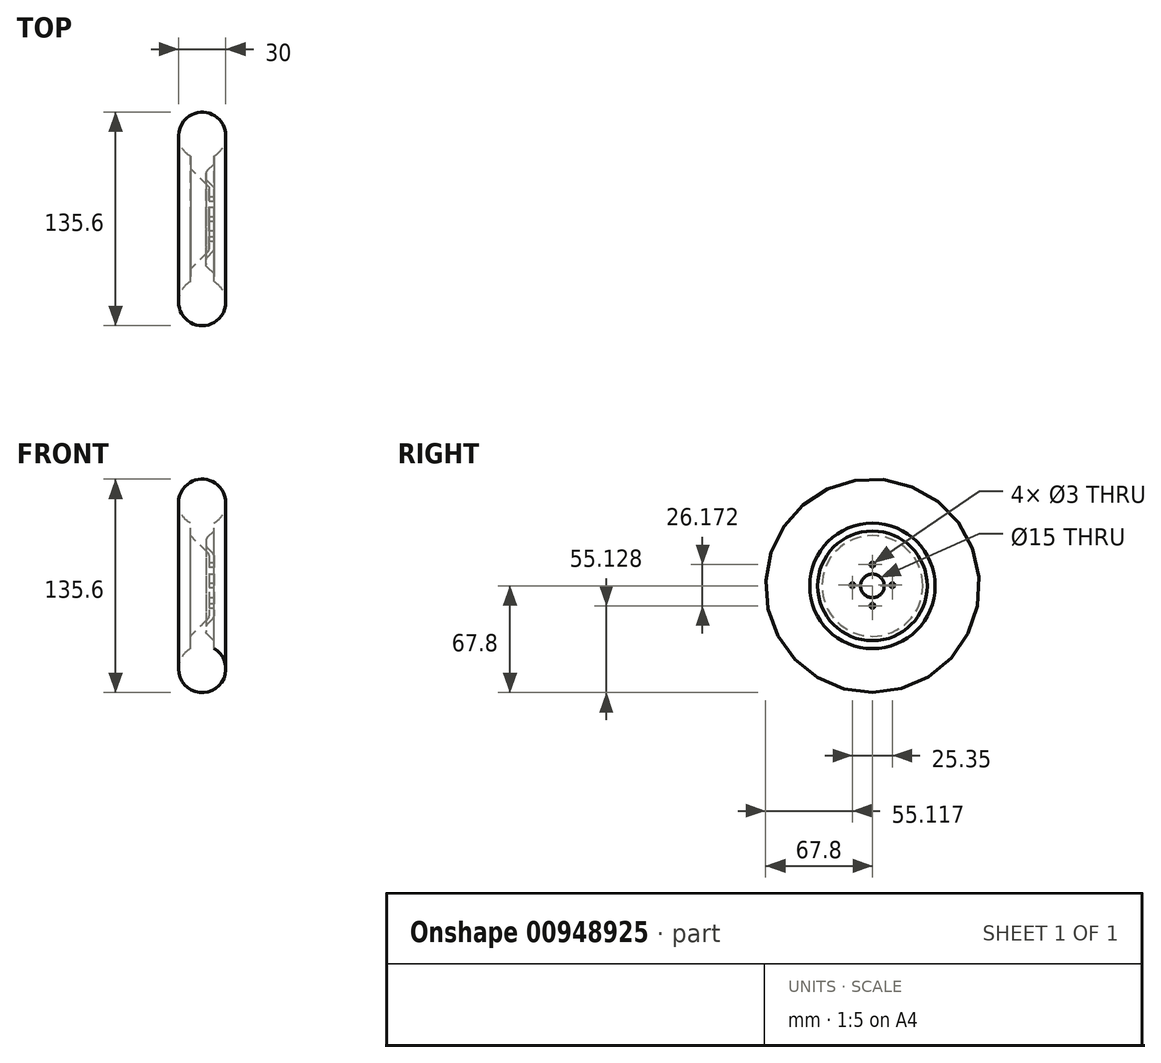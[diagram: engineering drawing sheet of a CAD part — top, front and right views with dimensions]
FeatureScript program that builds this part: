
annotation { "Feature Type Name" : "Feature", "Feature Type Description" : "" }
export const myFeature = defineFeature(function(context is Context, id is Id, definition is map)
    precondition{}
    {
        {
            var Q0;
            Q0=qCreatedBy(makeId("Front.planeOp"),FACE);
            var sketch = newSketch(context, id + "F0", { "sketchPlane" : qUnion([Q0])});
            skArc(sketch, "E0", {"start": v(-28.41, 19.81) * mm, "mid": v(-35.91, 47.8) * mm, "end": v(-43.41, 19.81) * mm});
            skLineSegment(sketch, "E1", {"start": v(-28.41, 19.81) * mm, "end": v(-28.41, 14.81) * mm});
            skLineSegment(sketch, "E2", {"start": v(-33.41, 10) * mm, "end": v(-28.41, 14.81) * mm});
            skLineSegment(sketch, "E3", {"start": v(-33.41, 10) * mm, "end": v(-33.41, 5) * mm});
            skPoint(sketch, "E4.end.orphan", {"position": v(-26.27, 0) * mm});
            skLineSegment(sketch, "E5", {"start": v(-33.41, 5) * mm, "end": v(-28.41, 0) * mm});
            skPoint(sketch, "E6.orphan", {"position": v(-26.27, -38.05) * mm});
            skPoint(sketch, "E7.end.orphan", {"position": v(-37, -38.05) * mm});
            skLineSegment(sketch, "E8", {"start": v(-28.41, 0) * mm, "end": v(-28.41, -20) * mm});
            skLineSegment(sketch, "E9", {"start": v(-61.22, -38.05) * mm, "end": v(-62.94, -38.85) * mm});
            skLineSegment(sketch, "E10", {"start": v(-66.63, -25.87) * mm, "end": v(-67.05, -27.37) * mm});
            skPoint(sketch, "E11.start.orphan", {"position": v(-66.63, -34.7) * mm});
            skPoint(sketch, "E12.end.orphan", {"position": v(-61.22, -34.7) * mm});
            skPoint(sketch, "E13.start.orphan", {"position": v(-37, -25.87) * mm});
            skPoint(sketch, "E14.start.orphan", {"position": v(-47.29, -25.87) * mm});
            skLineSegment(sketch, "E15", {"start": v(-31.41, 0) * mm, "end": v(-31.41, -1.87) * mm});
            skLineSegment(sketch, "E16", {"start": v(-31.41, 0) * mm, "end": v(-43.41, 12) * mm});
            skPoint(sketch, "E17.end.orphan", {"position": v(-52.58, -10.52) * mm});
            skPoint(sketch, "E18.start.orphan", {"position": v(-52.58, -29.68) * mm});
            skLineSegment(sketch, "E19", {"start": v(-28.41, -20) * mm, "end": v(-31.41, -20) * mm});
            skLineSegment(sketch, "E20", {"start": v(-31.41, -20) * mm, "end": v(-31.41, -1.87) * mm});
            skPoint(sketch, "E21.end.orphan", {"position": v(-53, -1.87) * mm});
            skPoint(sketch, "E22.start.orphan", {"position": v(-43.41, 14.81) * mm});
            skLineSegment(sketch, "E23", {"start": v(-43.41, 19.81) * mm, "end": v(-43.41, 12) * mm});
            skPoint(sketch, "E24.start.orphan", {"position": v(-28.41, 32.8) * mm});
            skSolve(sketch);
        }
        {
            var Q0;
            Q0=makeQuery(id+"F0.imprint","IMPRINT",FACE,{"disambiguationData":[TD([[makeQuery(id+"F0.imprint","IMPRINT",EDGE,{"derivedFrom":sQuery(id+"F0.wireOp",EDGE,"ig5zt77j-EQ4V-wuMH-9RIN-2pZxivVrfX0F")}),-1.0]])]});
            var Q1;
            Q1=makeQuery(id+"F0.imprint","IMPRINT",FACE,{"disambiguationData":[TD([[makeQuery(id+"F0.imprint","IMPRINT",EDGE,{"derivedFrom":sQuery(id+"F0.wireOp",EDGE,"ig5zt77j-EQ4V-wuMH-9RIN-2pZxivVrfX0F")}),1.0]])]});
            var Q2;
            Q2=makeQuery(id+"F0.imprint","IMPRINT",FACE,{"disambiguationData":[TD([[makeQuery(id+"F0.imprint","IMPRINT",EDGE,{"derivedFrom":sQuery(id+"F0.wireOp",EDGE,"P19UumjC-ikMn-kLLg-niX1-3UejyW5Ps7u9")}),1.0]])]});
            var Q3;
            Q3=makeQuery(id+"F0.imprint","IMPRINT",FACE,{"disambiguationData":[TD([[makeQuery(id+"F0.imprint","IMPRINT",EDGE,{"derivedFrom":sQuery(id+"F0.wireOp",EDGE,"E8")}),-1.0]])]});
            var Q4;
            Q4=sQuery(id+"F0.wireOp",EDGE,"E19");
            revolve(context, id + "F1", {"surfaceOperationType" : NewSurfaceOperationType.NEW, "entities" : qUnion([Q0, Q1, Q2, Q3]), "axis" : qUnion([Q4]), "revolveType" : RevolveType.FULL});
        }
        {
            var Q0;
            Q0=makeQuery(id+"F1.opRevolve","SWEPT_EDGE",EDGE,{"disambiguationData":[OSD([sQuery(id+"F0.wireOp",EDGE,"E2"),sQuery(id+"F0.wireOp",EDGE,"E3")])]});
            var Q1;
            Q1=makeQuery(id+"F1.opRevolve","SWEPT_EDGE",EDGE,{"disambiguationData":[OSD([sQuery(id+"F0.wireOp",EDGE,"E5"),sQuery(id+"F0.wireOp",EDGE,"E8")])]});
            fillet(context, id + "F2", {"entities" : qUnion([Q0, Q1]), "radius" : 2 * mm, "tangentPropagation" : true, "allowEdgeOverflow" : false});
        }
        {
            var Q0;
            Q0=makeQuery(id+"F1.opRevolve","SWEPT_FACE",FACE,{"disambiguationData":[OSD([sQuery(id+"F0.wireOp",EDGE,"E8")])]});
            var sketch = newSketch(context, id + "F3", { "sketchPlane" : qUnion([Q0])});
            skLineSegment(sketch, "E25", {"start": v(0, 0) * mm, "end": v(0, -20) * mm});
            skCircle(sketch, "E26", {"center": v(0, -20) * mm, "radius": 7.5 * mm});
            skSolve(sketch);
        }
        {
            var Q0;
            Q0=makeQuery(id+"F1.opRevolve","SWEPT_EDGE",EDGE,{"disambiguationData":[OSD([sQuery(id+"F0.wireOp",EDGE,"E3"),sQuery(id+"F0.wireOp",EDGE,"E5")])]});
            fillet(context, id + "F4", {"entities" : qUnion([Q0]), "radius" : 1.9 * mm, "tangentPropagation" : true, "allowEdgeOverflow" : false});
        }
        {
            var Q0;
            Q0=sQuery(id+"F3.wireOp",VERTEX,"E25.end");
            var Q1;
            Q1=makeQuery(id+"F1.opRevolve","SWEPT_BODY",BODY,{"disambiguationData":[OSD([sQuery(id+"F0.wireOp",EDGE,"E0"),sQuery(id+"F0.wireOp",EDGE,"E1"),sQuery(id+"F0.wireOp",EDGE,"E2"),sQuery(id+"F0.wireOp",EDGE,"E3"),sQuery(id+"F0.wireOp",EDGE,"E5"),sQuery(id+"F0.wireOp",EDGE,"E8"),sQuery(id+"F0.wireOp",EDGE,"E15"),sQuery(id+"F0.wireOp",EDGE,"E16"),sQuery(id+"F0.wireOp",EDGE,"E19"),sQuery(id+"F0.wireOp",EDGE,"E20"),sQuery(id+"F0.wireOp",EDGE,"E23")])]});
            hole(context, id + "F5", {"style" : HoleStyle.SIMPLE, "endStyle" : HoleEndStyle.THROUGH, "holeDiameter" : 15 * mm, "majorDiameter" : 5 * mm, "isTappedThrough" : true, "tappedDepth" : 12 * mm, "tapClearance" : 3, "locations" : qUnion([Q0]), "scope" : qUnion([Q1])});
        }
        {
            var Q0;
            Q0=qCreatedBy(makeId("Right.planeOp"),FACE);
            var sketch = newSketch(context, id + "F6", { "sketchPlane" : qUnion([Q0])});
            skLineSegment(sketch, "E27", {"start": v(0, -5) * mm, "end": v(0, -6.5) * mm});
            skLineSegment(sketch, "E28", {"start": v(0, -34.12) * mm, "end": v(0, -32.62) * mm});
            skLineSegment(sketch, "E29", {"start": v(0, -32.62) * mm, "end": v(0, -31.12) * mm});
            skLineSegment(sketch, "E30", {"start": v(-14.18, -19.56) * mm, "end": v(-12.68, -19.56) * mm});
            skLineSegment(sketch, "E31", {"start": v(14.13, -19.56) * mm, "end": v(12.63, -19.56) * mm});
            skCircle(sketch, "E32", {"center": v(0, -6.5) * mm, "radius": 1.5 * mm});
            skCircle(sketch, "E33", {"center": v(-12.68, -19.56) * mm, "radius": 1.5 * mm});
            skCircle(sketch, "E34", {"center": v(0, -32.62) * mm, "radius": 1.5 * mm});
            skCircle(sketch, "E35", {"center": v(12.63, -19.56) * mm, "radius": 1.5 * mm});
            skPoint(sketch, "E36.orphan", {"position": v(-19.18, -19.56) * mm});
            skPoint(sketch, "E37.orphan", {"position": v(0, -39.12) * mm});
            skPoint(sketch, "E38.orphan", {"position": v(19.13, -19.56) * mm});
            skPoint(sketch, "E39.end.orphan", {"position": v(0, -19.56) * mm});
            skLineSegment(sketch, "E40.trimOffspring", {"start": v(0, -8) * mm, "end": v(0, -6.5) * mm});
            skSolve(sketch);
        }
        {
            var Q0;
            Q0=sQuery(id+"F6.wireOp",VERTEX,"E27.end");
            var Q1;
            Q1=sQuery(id+"F6.wireOp",VERTEX,"E30.end");
            var Q2;
            Q2=makeQuery(id+"F1.opRevolve","SWEPT_BODY",BODY,{"disambiguationData":[OSD([sQuery(id+"F0.wireOp",EDGE,"E0"),sQuery(id+"F0.wireOp",EDGE,"E1"),sQuery(id+"F0.wireOp",EDGE,"E2"),sQuery(id+"F0.wireOp",EDGE,"E3"),sQuery(id+"F0.wireOp",EDGE,"E5"),sQuery(id+"F0.wireOp",EDGE,"E8"),sQuery(id+"F0.wireOp",EDGE,"E15"),sQuery(id+"F0.wireOp",EDGE,"E16"),sQuery(id+"F0.wireOp",EDGE,"E19"),sQuery(id+"F0.wireOp",EDGE,"E20"),sQuery(id+"F0.wireOp",EDGE,"E23")])]});
            hole(context, id + "F7", {"style" : HoleStyle.SIMPLE, "endStyle" : HoleEndStyle.THROUGH, "holeDiameter" : 3 * mm, "majorDiameter" : 5 * mm, "isTappedThrough" : true, "tappedDepth" : 12 * mm, "tapClearance" : 3, "locations" : qUnion([Q0, Q1]), "scope" : qUnion([Q2])});
        }
        {
            var Q0;
            Q0=makeQuery(id+"F1.opRevolve","SWEPT_FACE",FACE,{"disambiguationData":[OSD([sQuery(id+"F0.wireOp",EDGE,"E8")])]});
            var sketch = newSketch(context, id + "F8", { "sketchPlane" : qUnion([Q0])});
            skPoint(sketch, "E41.start.orphan", {"position": v(0, -39.17) * mm});
            skLineSegment(sketch, "E42", {"start": v(0, -8) * mm, "end": v(0, -39.17) * mm});
            skLineSegment(sketch, "E43", {"start": v(0, -34.17) * mm, "end": v(0, -32.67) * mm});
            skLineSegment(sketch, "E44", {"start": v(-12.68, -19.56) * mm, "end": v(14.17, -19.56) * mm});
            skLineSegment(sketch, "E45", {"start": v(14.17, -19.56) * mm, "end": v(12.67, -19.56) * mm});
            skCircle(sketch, "E46", {"center": v(0, -32.67) * mm, "radius": 1.5 * mm});
            skCircle(sketch, "E47", {"center": v(12.67, -19.56) * mm, "radius": 1.5 * mm});
            skSolve(sketch);
        }
        {
            var Q0;
            Q0=sQuery(id+"F8.wireOp",VERTEX,"E43.end");
            var Q1;
            Q1=makeQuery(id+"F1.opRevolve","SWEPT_BODY",BODY,{"disambiguationData":[OSD([sQuery(id+"F0.wireOp",EDGE,"E0"),sQuery(id+"F0.wireOp",EDGE,"E1"),sQuery(id+"F0.wireOp",EDGE,"E2"),sQuery(id+"F0.wireOp",EDGE,"E3"),sQuery(id+"F0.wireOp",EDGE,"E5"),sQuery(id+"F0.wireOp",EDGE,"E8"),sQuery(id+"F0.wireOp",EDGE,"E15"),sQuery(id+"F0.wireOp",EDGE,"E16"),sQuery(id+"F0.wireOp",EDGE,"E19"),sQuery(id+"F0.wireOp",EDGE,"E20"),sQuery(id+"F0.wireOp",EDGE,"E23")])]});
            hole(context, id + "F9", {"style" : HoleStyle.SIMPLE, "endStyle" : HoleEndStyle.THROUGH, "holeDiameter" : 3 * mm, "majorDiameter" : 5 * mm, "isTappedThrough" : true, "tappedDepth" : 12 * mm, "tapClearance" : 3, "locations" : qUnion([Q0]), "scope" : qUnion([Q1])});
        }
        {
            var Q0;
            Q0=makeQuery(id+"F1.opRevolve","SWEPT_FACE",FACE,{"disambiguationData":[OSD([sQuery(id+"F0.wireOp",EDGE,"E8")])]});
            var sketch = newSketch(context, id + "F10", { "sketchPlane" : qUnion([Q0])});
            skLineSegment(sketch, "E48", {"start": v(12.67, -19.56) * mm, "end": v(14.17, -19.56) * mm});
            skLineSegment(sketch, "E49", {"start": v(14.17, -19.56) * mm, "end": v(12.67, -19.56) * mm});
            skPoint(sketch, "E50.orphan", {"position": v(-12.68, -19.56) * mm});
            skCircle(sketch, "E51", {"center": v(12.67, -19.56) * mm, "radius": 1.5 * mm});
            skSolve(sketch);
        }
        {
            var Q0;
            Q0=sQuery(id+"F10.wireOp",VERTEX,"E48.start");
            var Q1;
            Q1=makeQuery(id+"F1.opRevolve","SWEPT_BODY",BODY,{"disambiguationData":[OSD([sQuery(id+"F0.wireOp",EDGE,"E0"),sQuery(id+"F0.wireOp",EDGE,"E1"),sQuery(id+"F0.wireOp",EDGE,"E2"),sQuery(id+"F0.wireOp",EDGE,"E3"),sQuery(id+"F0.wireOp",EDGE,"E5"),sQuery(id+"F0.wireOp",EDGE,"E8"),sQuery(id+"F0.wireOp",EDGE,"E15"),sQuery(id+"F0.wireOp",EDGE,"E16"),sQuery(id+"F0.wireOp",EDGE,"E19"),sQuery(id+"F0.wireOp",EDGE,"E20"),sQuery(id+"F0.wireOp",EDGE,"E23")])]});
            hole(context, id + "F11", {"style" : HoleStyle.SIMPLE, "endStyle" : HoleEndStyle.THROUGH, "holeDiameter" : 3 * mm, "majorDiameter" : 5 * mm, "isTappedThrough" : true, "tappedDepth" : 12 * mm, "tapClearance" : 3, "locations" : qUnion([Q0]), "scope" : qUnion([Q1])});
        }
        {
            var Q0;
            Q0=makeQuery(id+"F1.opRevolve","SWEPT_EDGE",EDGE,{"disambiguationData":[OSD([sQuery(id+"F0.wireOp",EDGE,"E15"),sQuery(id+"F0.wireOp",EDGE,"E16")])]});
            fillet(context, id + "F12", {"entities" : qUnion([Q0]), "radius" : 1.8 * mm, "tangentPropagation" : true, "allowEdgeOverflow" : false});
        }
    });
